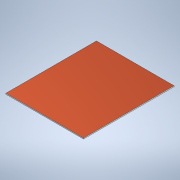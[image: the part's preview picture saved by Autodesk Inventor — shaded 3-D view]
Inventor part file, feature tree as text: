
AUTODESK INVENTOR PART (.ipt)
format: ipt  version: 2020 (Build 240168000, 168)  size: 98,816 bytes
history: native  units: mm
features: other x1, extrude x1, sketch x1
ambient origin geometry x8: Origin, YZ Plane, XZ Plane, XY Plane, X Axis, Y Axis, Z Axis, Center Point
bodies: Body1 (feature_tree)
feature tree (3):
  other  "Sólido1"
  extrude  "Extrusión1"  Depth=1.0mm TaperAngle=0.0deg
  sketch  "Boceto1"  dims[d3=45.5mm d4=1.0mm d5=0.0mm d7=39.0mm]
